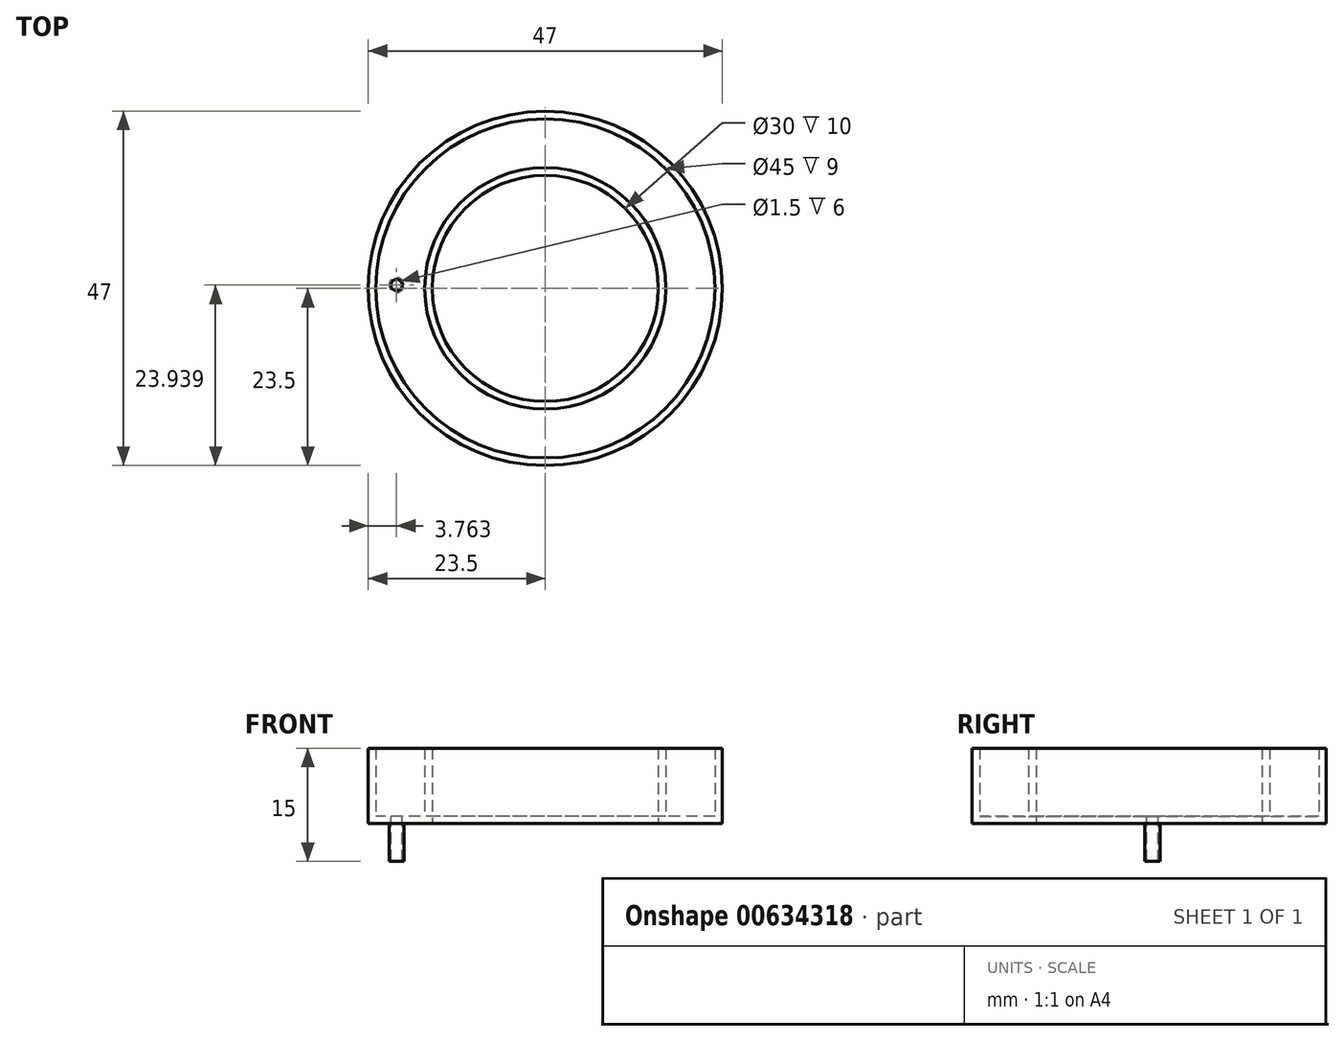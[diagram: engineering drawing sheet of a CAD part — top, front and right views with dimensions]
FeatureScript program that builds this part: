
annotation { "Feature Type Name" : "Feature", "Feature Type Description" : "" }
export const myFeature = defineFeature(function(context is Context, id is Id, definition is map)
    precondition{}
    {
        {
            var Q0;
            Q0=qCreatedBy(makeId("Top.planeOp"),FACE);
            var sketch = newSketch(context, id + "F0", { "sketchPlane" : qUnion([Q0])});
            skCircle(sketch, "E0", {"center": v(0, 0) * mm, "radius": 23.5 * mm});
            skCircle(sketch, "E1", {"center": v(0, 0) * mm, "radius": 15 * mm});
            skSolve(sketch);
        }
        {
            var Q0;
            Q0=makeQuery(id+"F0.imprint","IMPRINT",FACE,{"disambiguationData":[TD([[makeQuery(id+"F0.imprint","IMPRINT",EDGE,{"derivedFrom":sQuery(id+"F0.wireOp",EDGE,"E0")}),1.0]])]});
            extrude(context, id + "F1", {"entities" : qUnion([Q0]), "depth" : 10 * mm, "offsetDistance" : 25.4 * mm});
        }
        {
            var Q0;
            Q0=makeQuery(id+"F1.opExtrude","CAP_FACE",FACE,{"disambiguationData":[OSD([sQuery(id+"F0.wireOp",EDGE,"E0"),sQuery(id+"F0.wireOp",EDGE,"E1")])],"isStart":false});
            shell(context, id + "F2", {"entities" : qUnion([Q0]), "thickness" : 1 * mm});
        }
        {
            var Q0;
            Q0=makeQuery(id+"F1.opExtrude","CAP_FACE",FACE,{"disambiguationData":[OSD([sQuery(id+"F0.wireOp",EDGE,"E0"),sQuery(id+"F0.wireOp",EDGE,"E1")])],"isStart":true});
            var sketch = newSketch(context, id + "F3", { "sketchPlane" : qUnion([Q0])});
            skCircle(sketch, "E2", {"center": v(-19.74, -0.44) * mm, "radius": 1 * mm});
            skCircle(sketch, "E3", {"center": v(-19.74, -0.44) * mm, "radius": 0.75 * mm});
            skSolve(sketch);
        }
        {
            var Q0;
            Q0=makeQuery(id+"F3.imprint","IMPRINT",FACE,{"disambiguationData":[TD([[makeQuery(id+"F3.imprint","IMPRINT",EDGE,{"derivedFrom":sQuery(id+"F3.wireOp",EDGE,"E2")}),1.0]])]});
            extrude(context, id + "F4", {"entities" : qUnion([Q0]), "operationType" : NewBodyOperationType.ADD, "depth" : 5 * mm, "offsetDistance" : 25.4 * mm});
        }
        {
            var Q0;
            Q0=makeQuery(id+"F3.imprint","IMPRINT",FACE,{"disambiguationData":[TD([[makeQuery(id+"F3.imprint","IMPRINT",EDGE,{"derivedFrom":sQuery(id+"F3.wireOp",EDGE,"E2")}),-1.0]])]});
            var sketch = newSketch(context, id + "F5", { "sketchPlane" : qUnion([Q0])});
            skCircle(sketch, "E4", {"center": v(-19.74, -0.44) * mm, "radius": 0.75 * mm});
            skSolve(sketch);
        }
        {
            var Q0;
            Q0 = qSketchRegion(id + "F5", true);
            extrude(context, id + "F6", {"entities" : qUnion([Q0]), "operationType" : NewBodyOperationType.REMOVE, "oppositeDirection" : true, "depth" : 1.1 * mm, "offsetDistance" : 25.4 * mm});
        }
    });
